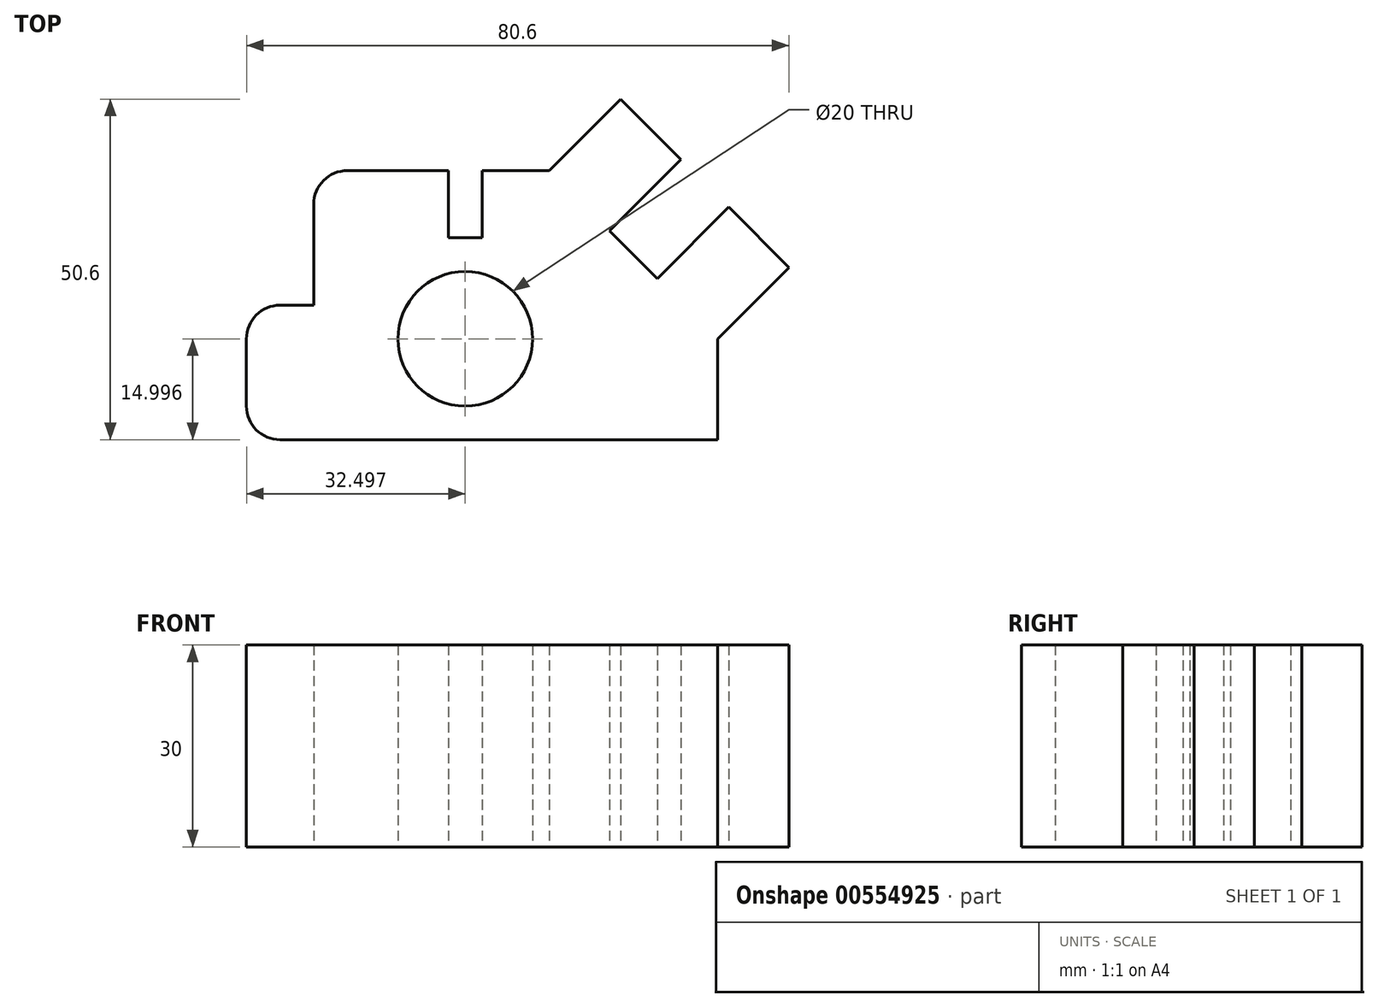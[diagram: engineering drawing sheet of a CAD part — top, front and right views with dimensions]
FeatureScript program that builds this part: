
annotation { "Feature Type Name" : "Feature", "Feature Type Description" : "" }
export const myFeature = defineFeature(function(context is Context, id is Id, definition is map)
    precondition{}
    {
        {
            var Q0;
            Q0=qCreatedBy(makeId("Top.planeOp"),FACE);
            var sketch = newSketch(context, id + "F0", { "sketchPlane" : qUnion([Q0])});
            skLineSegment(sketch, "E0", {"start": v(-19.06, -27.05) * mm, "end": v(45.94, -27.05) * mm});
            skLineSegment(sketch, "E1", {"start": v(-24.06, -22.05) * mm, "end": v(-24.06, -12.05) * mm});
            skLineSegment(sketch, "E2", {"start": v(-19.06, -7.05) * mm, "end": v(-14.06, -7.05) * mm});
            skLineSegment(sketch, "E3", {"start": v(-14.06, -7.05) * mm, "end": v(-14.06, 7.95) * mm});
            skLineSegment(sketch, "E4", {"start": v(-9.06, 12.95) * mm, "end": v(5.94, 12.95) * mm});
            skLineSegment(sketch, "E5", {"start": v(5.94, 12.95) * mm, "end": v(5.94, 2.95) * mm});
            skLineSegment(sketch, "E6", {"start": v(5.94, 2.95) * mm, "end": v(10.94, 2.95) * mm});
            skLineSegment(sketch, "E7", {"start": v(10.94, 2.95) * mm, "end": v(10.94, 12.95) * mm});
            skLineSegment(sketch, "E8", {"start": v(10.94, 12.95) * mm, "end": v(20.94, 12.95) * mm});
            skLineSegment(sketch, "E9", {"start": v(45.94, -27.05) * mm, "end": v(45.94, -12.05) * mm});
            skLineSegment(sketch, "E10", {"start": v(29.9, 3.98) * mm, "end": v(40.5, 14.59) * mm});
            skPoint(sketch, "E11.start.orphan", {"position": v(33.44, 0.45) * mm});
            skLineSegment(sketch, "E12", {"start": v(20.94, 12.95) * mm, "end": v(31.54, 23.55) * mm});
            skLineSegment(sketch, "E13", {"start": v(31.54, 23.55) * mm, "end": v(40.5, 14.59) * mm});
            skLineSegment(sketch, "E14", {"start": v(45.94, -12.05) * mm, "end": v(56.54, -1.45) * mm});
            skPoint(sketch, "E15.end.orphan", {"position": v(40.5, 0.45) * mm});
            skLineSegment(sketch, "E16", {"start": v(36.97, -3.09) * mm, "end": v(47.58, 7.52) * mm});
            skLineSegment(sketch, "E17", {"start": v(47.58, 7.52) * mm, "end": v(56.54, -1.45) * mm});
            skLineSegment(sketch, "E18", {"start": v(29.9, 3.98) * mm, "end": v(36.97, -3.09) * mm});
            skCircle(sketch, "E19", {"center": v(8.44, -12.05) * mm, "radius": 10 * mm});
            skPoint(sketch, "E20.visualSharp", {"position": v(-24.06, -7.05) * mm});
            skArc(sketch, "E20.filletArc", {"start": v(-19.06, -7.05) * mm, "mid": v(-22.6, -8.52) * mm, "end": v(-24.06, -12.05) * mm});
            skPoint(sketch, "E21.visualSharp", {"position": v(-24.06, -27.05) * mm});
            skArc(sketch, "E21.filletArc", {"start": v(-24.06, -22.05) * mm, "mid": v(-22.6, -25.59) * mm, "end": v(-19.06, -27.05) * mm});
            skPoint(sketch, "E22.visualSharp", {"position": v(-14.06, 12.95) * mm});
            skArc(sketch, "E22.filletArc", {"start": v(-9.06, 12.95) * mm, "mid": v(-12.6, 11.48) * mm, "end": v(-14.06, 7.95) * mm});
            skSolve(sketch);
        }
        {
            var Q0;
            Q0=makeQuery(id+"F0.imprint","IMPRINT",FACE,{"disambiguationData":[TD([[makeQuery(id+"F0.imprint","IMPRINT",EDGE,{"derivedFrom":sQuery(id+"F0.wireOp",EDGE,"E0")}),1.0]])]});
            extrude(context, id + "F1", {"entities" : qUnion([Q0]), "depth" : 30 * mm, "offsetDistance" : 25 * mm});
        }
    });
